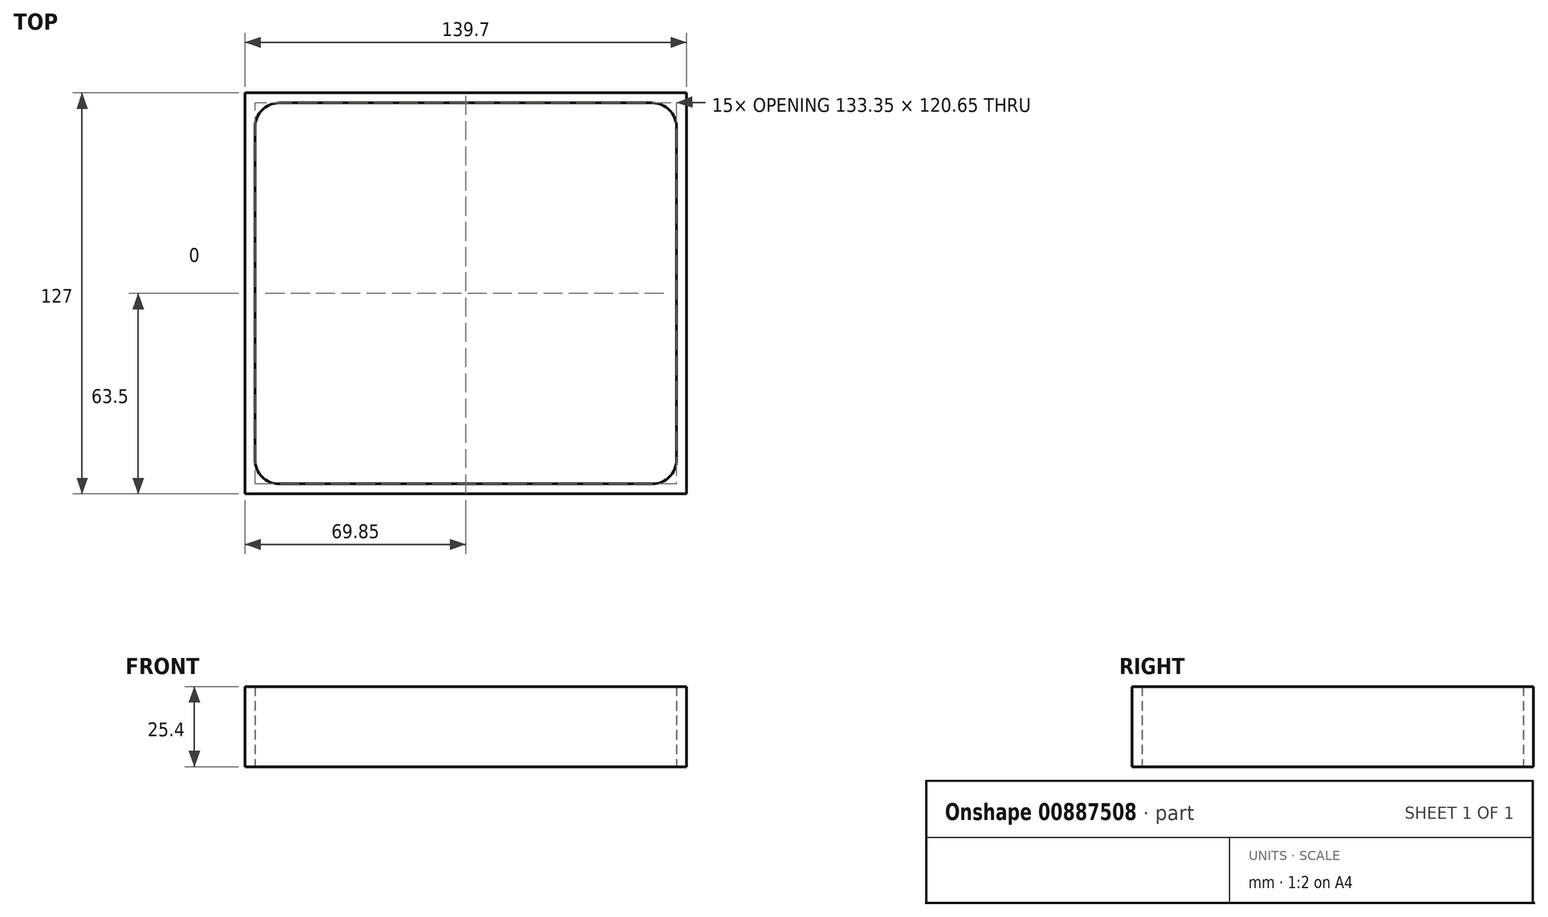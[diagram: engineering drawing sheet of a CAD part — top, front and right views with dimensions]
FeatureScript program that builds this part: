
annotation { "Feature Type Name" : "Feature", "Feature Type Description" : "" }
export const myFeature = defineFeature(function(context is Context, id is Id, definition is map)
    precondition{}
    {
        {
            var Q0;
            Q0=qCreatedBy(makeId("Top.planeOp"),FACE);
            var sketch = newSketch(context, id + "F0", { "sketchPlane" : qUnion([Q0])});
            skLineSegment(sketch, "E0.bottom", {"start": v(-69.85, 63.5) * mm, "end": v(69.85, 63.5) * mm});
            skLineSegment(sketch, "E0.top", {"start": v(-69.85, -63.5) * mm, "end": v(69.85, -63.5) * mm});
            skLineSegment(sketch, "E0.left", {"start": v(-69.85, 63.5) * mm, "end": v(-69.85, -63.5) * mm});
            skLineSegment(sketch, "E0.right", {"start": v(69.85, 63.5) * mm, "end": v(69.85, -63.5) * mm});
            skPoint(sketch, "E0.middle", {"position": v(0, 0) * mm});
            skLineSegment(sketch, "E1.bottom", {"start": v(-66.68, 60.33) * mm, "end": v(66.68, 60.33) * mm});
            skLineSegment(sketch, "E1.top", {"start": v(-66.68, -60.33) * mm, "end": v(66.68, -60.33) * mm});
            skLineSegment(sketch, "E1.left", {"start": v(-66.67, 60.33) * mm, "end": v(-66.68, -60.33) * mm});
            skLineSegment(sketch, "E1.right", {"start": v(66.68, 60.33) * mm, "end": v(66.68, -60.33) * mm});
            skLineSegment(sketch, "E2.bottom", {"start": v(-69.85, 63.5) * mm, "end": v(-44.45, 63.5) * mm});
            skLineSegment(sketch, "E2.top", {"start": v(-69.85, 38.1) * mm, "end": v(-44.45, 38.1) * mm});
            skLineSegment(sketch, "E2.left", {"start": v(-69.85, 63.5) * mm, "end": v(-69.85, 38.1) * mm});
            skLineSegment(sketch, "E2.right", {"start": v(-44.45, 63.5) * mm, "end": v(-44.45, 38.1) * mm});
            skSolve(sketch);
        }
        {
            var Q0;
            Q0 = qSketchRegion(id + "F0", true);
            extrude(context, id + "F1", {"entities" : qUnion([Q0]), "depth" : 25.4 * mm, "offsetDistance" : 25.4 * mm});
        }
        {
            var Q0;
            Q0=makeQuery(id+"F1.opExtrude","SWEPT_EDGE",EDGE,{"disambiguationData":[OSD([sQuery(id+"F0.wireOp",EDGE,"E1.bottom"),sQuery(id+"F0.wireOp",EDGE,"E1.right")])]});
            var Q1;
            Q1=makeQuery(id+"F1.opExtrude","SWEPT_EDGE",EDGE,{"disambiguationData":[OSD([sQuery(id+"F0.wireOp",EDGE,"E1.top"),sQuery(id+"F0.wireOp",EDGE,"E1.right")])]});
            var Q2;
            Q2=makeQuery(id+"F1.opExtrude","SWEPT_EDGE",EDGE,{"disambiguationData":[OSD([sQuery(id+"F0.wireOp",EDGE,"E1.top"),sQuery(id+"F0.wireOp",EDGE,"E1.left")])]});
            var Q3;
            Q3=makeQuery(id+"F1.opExtrude","SWEPT_EDGE",EDGE,{"disambiguationData":[OSD([sQuery(id+"F0.wireOp",EDGE,"E1.bottom"),sQuery(id+"F0.wireOp",EDGE,"E1.left")])]});
            fillet(context, id + "F2", {"entities" : qUnion([Q0, Q1, Q2, Q3]), "radius" : 7.62 * mm, "tangentPropagation" : true, "allowEdgeOverflow" : false});
        }
    });
